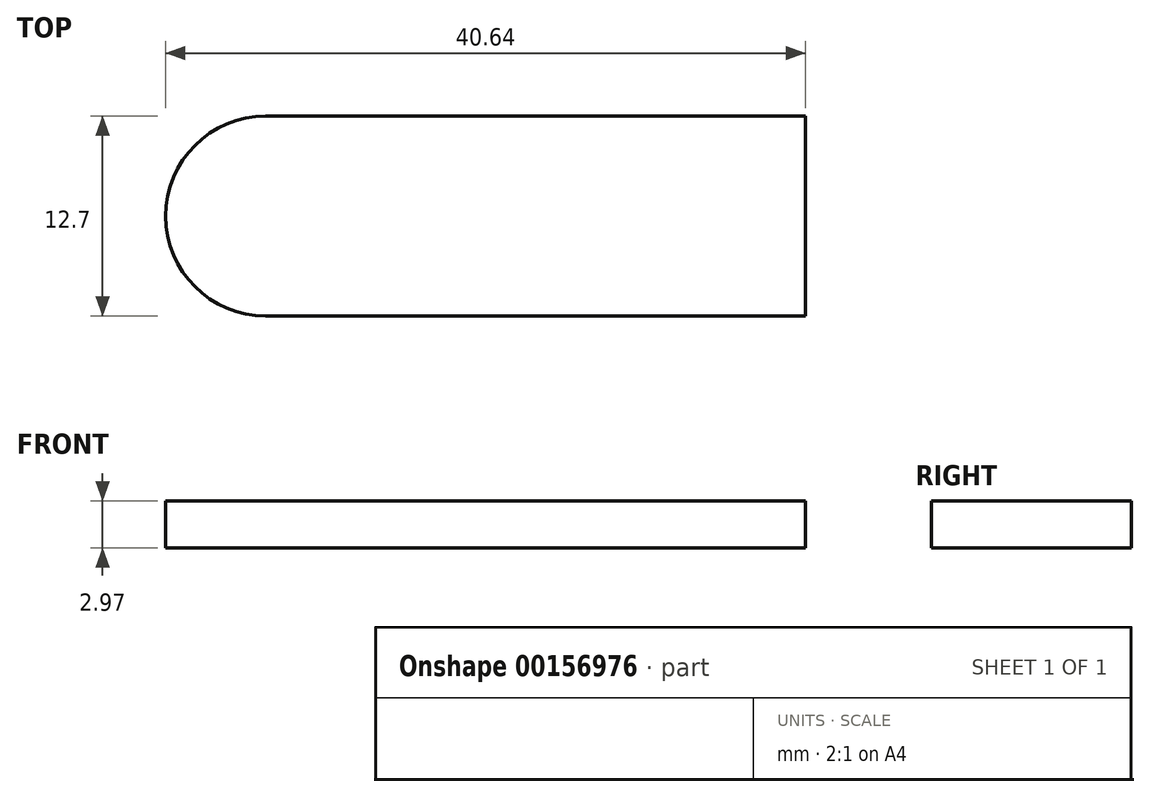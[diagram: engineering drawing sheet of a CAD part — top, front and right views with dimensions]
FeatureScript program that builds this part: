
annotation { "Feature Type Name" : "Feature", "Feature Type Description" : "" }
export const myFeature = defineFeature(function(context is Context, id is Id, definition is map)
    precondition{}
    {
        {
            var Q0;
            Q0=qCreatedBy(makeId("Top.planeOp"),FACE);
            var sketch = newSketch(context, id + "F0", { "sketchPlane" : qUnion([Q0])});
            skLineSegment(sketch, "E0.bottom", {"start": v(101.6, -57.15) * mm, "end": v(-101.6, -57.15) * mm});
            skLineSegment(sketch, "E0.top", {"start": v(101.6, 57.15) * mm, "end": v(-101.6, 57.15) * mm});
            skLineSegment(sketch, "E0.left", {"start": v(101.6, -57.15) * mm, "end": v(101.6, 57.15) * mm});
            skLineSegment(sketch, "E0.right", {"start": v(-101.6, -57.15) * mm, "end": v(-101.6, 57.15) * mm});
            skPoint(sketch, "E0.middle", {"position": v(0, 0) * mm});
            skLineSegment(sketch, "E1.bottom", {"start": v(88.9, -57.15) * mm, "end": v(78.74, -57.15) * mm});
            skLineSegment(sketch, "E1.top", {"start": v(88.9, -62.23) * mm, "end": v(78.74, -62.23) * mm});
            skLineSegment(sketch, "E1.left", {"start": v(88.9, -57.15) * mm, "end": v(88.9, -62.23) * mm});
            skLineSegment(sketch, "E1.right", {"start": v(78.74, -57.15) * mm, "end": v(78.74, -62.23) * mm});
            skLineSegment(sketch, "E2.1.0.0", {"start": v(12.7, -57.15) * mm, "end": v(12.7, -62.23) * mm});
            skLineSegment(sketch, "E2.1.0.1", {"start": v(12.7, -62.23) * mm, "end": v(2.54, -62.23) * mm});
            skLineSegment(sketch, "E2.1.0.2", {"start": v(2.54, -57.15) * mm, "end": v(2.54, -62.23) * mm});
            skLineSegment(sketch, "E2.1.0.3", {"start": v(12.7, -57.15) * mm, "end": v(2.54, -57.15) * mm});
            skLineSegment(sketch, "E2.2.0.0", {"start": v(-63.5, -57.15) * mm, "end": v(-63.5, -62.23) * mm});
            skLineSegment(sketch, "E2.2.0.1", {"start": v(-63.5, -62.23) * mm, "end": v(-73.66, -62.23) * mm});
            skLineSegment(sketch, "E2.2.0.2", {"start": v(-73.66, -57.15) * mm, "end": v(-73.66, -62.23) * mm});
            skLineSegment(sketch, "E2.2.0.3", {"start": v(-63.5, -57.15) * mm, "end": v(-73.66, -57.15) * mm});
            skLineSegment(sketch, "E2.direction1", {"start": v(88.9, -62.23) * mm, "end": v(12.7, -62.23) * mm, "construction": true});
            skLineSegment(sketch, "E3.MirrorCS", {"start": v(-63.5, 57.15) * mm, "end": v(-63.5, 62.23) * mm});
            skLineSegment(sketch, "E4.MirrorCS", {"start": v(-63.5, 62.23) * mm, "end": v(-73.66, 62.23) * mm});
            skLineSegment(sketch, "E5.MirrorCS", {"start": v(-73.66, 57.15) * mm, "end": v(-73.66, 62.23) * mm});
            skLineSegment(sketch, "E6.MirrorCS", {"start": v(2.54, 57.15) * mm, "end": v(2.54, 62.23) * mm});
            skLineSegment(sketch, "E7.MirrorCS", {"start": v(12.7, 62.23) * mm, "end": v(2.54, 62.23) * mm});
            skLineSegment(sketch, "E8.MirrorCS", {"start": v(12.7, 57.15) * mm, "end": v(12.7, 62.23) * mm});
            skLineSegment(sketch, "E9.MirrorCS", {"start": v(78.74, 57.15) * mm, "end": v(78.74, 62.23) * mm});
            skLineSegment(sketch, "E10.MirrorCS", {"start": v(88.9, 62.23) * mm, "end": v(12.7, 62.23) * mm, "construction": true});
            skLineSegment(sketch, "E11.MirrorCS", {"start": v(88.9, 57.15) * mm, "end": v(88.9, 62.23) * mm});
            skLineSegment(sketch, "E12", {"start": v(88.9, 62.23) * mm, "end": v(78.74, 62.23) * mm});
            skSolve(sketch);
        }
        {
            var Q0;
            Q0 = qSketchRegion(id + "F0", true);
            extrude(context, id + "F1", {"entities" : qUnion([Q0]), "depth" : 2.97 * mm});
        }
        {
            var Q0;
            Q0=makeQuery(id+"F1.opExtrude","CAP_FACE",FACE,{"disambiguationData":[OSD([sQuery(id+"F0.wireOp",EDGE,"E0.bottom"),sQuery(id+"F0.wireOp",EDGE,"E0.top"),sQuery(id+"F0.wireOp",EDGE,"E0.left"),sQuery(id+"F0.wireOp",EDGE,"E0.right"),sQuery(id+"F0.wireOp",EDGE,"E1.top"),sQuery(id+"F0.wireOp",EDGE,"E1.left"),sQuery(id+"F0.wireOp",EDGE,"E1.right"),sQuery(id+"F0.wireOp",EDGE,"E2.1.0.0"),sQuery(id+"F0.wireOp",EDGE,"E2.1.0.1"),sQuery(id+"F0.wireOp",EDGE,"E2.1.0.2"),sQuery(id+"F0.wireOp",EDGE,"E2.2.0.0"),sQuery(id+"F0.wireOp",EDGE,"E2.2.0.1"),sQuery(id+"F0.wireOp",EDGE,"E2.2.0.2"),sQuery(id+"F0.wireOp",EDGE,"E3.MirrorCS"),sQuery(id+"F0.wireOp",EDGE,"E4.MirrorCS"),sQuery(id+"F0.wireOp",EDGE,"E5.MirrorCS"),sQuery(id+"F0.wireOp",EDGE,"E6.MirrorCS"),sQuery(id+"F0.wireOp",EDGE,"E7.MirrorCS"),sQuery(id+"F0.wireOp",EDGE,"E8.MirrorCS"),sQuery(id+"F0.wireOp",EDGE,"E9.MirrorCS"),sQuery(id+"F0.wireOp",EDGE,"E11.MirrorCS"),sQuery(id+"F0.wireOp",EDGE,"E12")])],"isStart":false});
            var sketch = newSketch(context, id + "F2", { "sketchPlane" : qUnion([Q0])});
            skLineSegment(sketch, "E13", {"start": v(0, 0) * mm, "end": v(-101.6, 0) * mm, "construction": true});
            skLineSegment(sketch, "E14", {"start": v(12.7, -49.53) * mm, "end": v(71.12, -49.53) * mm});
            skArc(sketch, "E15.0.startCap", {"start": v(12.7, -54.61) * mm, "mid": v(7.62, -49.53) * mm, "end": v(12.7, -44.45) * mm});
            skArc(sketch, "E15.0.endCap", {"start": v(71.12, -44.45) * mm, "mid": v(76.2, -49.53) * mm, "end": v(71.12, -54.6) * mm});
            skLineSegment(sketch, "E15.0.left", {"start": v(12.7, -44.45) * mm, "end": v(71.12, -44.45) * mm});
            skLineSegment(sketch, "E15.0.right", {"start": v(12.7, -54.61) * mm, "end": v(71.12, -54.6) * mm});
            skLineSegment(sketch, "E16.MirrorCS", {"start": v(12.7, 44.45) * mm, "end": v(71.12, 44.45) * mm});
            skLineSegment(sketch, "E17.MirrorCS", {"start": v(12.7, 54.61) * mm, "end": v(71.12, 54.61) * mm});
            skArc(sketch, "E18.MirrorCS", {"start": v(12.7, 54.61) * mm, "mid": v(7.62, 49.53) * mm, "end": v(12.7, 44.45) * mm});
            skArc(sketch, "E19.MirrorCS", {"start": v(71.12, 44.45) * mm, "mid": v(76.2, 49.53) * mm, "end": v(71.12, 54.61) * mm});
            skLineSegment(sketch, "E20.MirrorCS", {"start": v(12.7, 49.53) * mm, "end": v(71.12, 49.53) * mm});
            skLineSegment(sketch, "E21", {"start": v(41.91, -49.53) * mm, "end": v(41.91, 0) * mm, "construction": true});
            skLineSegment(sketch, "E22.bottom", {"start": v(41.91, -44.45) * mm, "end": v(54.61, -44.45) * mm});
            skLineSegment(sketch, "E22.top", {"start": v(41.91, -36.83) * mm, "end": v(54.61, -36.83) * mm});
            skLineSegment(sketch, "E22.left", {"start": v(41.91, -44.45) * mm, "end": v(41.91, -36.83) * mm});
            skLineSegment(sketch, "E22.right", {"start": v(54.61, -44.45) * mm, "end": v(54.61, -36.83) * mm});
            skLineSegment(sketch, "E23.MirrorCS", {"start": v(29.2, -44.45) * mm, "end": v(29.2, -36.83) * mm});
            skLineSegment(sketch, "E24.MirrorCS", {"start": v(41.91, -36.83) * mm, "end": v(29.2, -36.83) * mm});
            skLineSegment(sketch, "E25", {"start": v(0, 0) * mm, "end": v(76.3, 0) * mm, "construction": true});
            skLineSegment(sketch, "E26.MirrorCS", {"start": v(41.91, 36.83) * mm, "end": v(29.2, 36.83) * mm});
            skLineSegment(sketch, "E27.MirrorCS", {"start": v(29.2, 44.45) * mm, "end": v(29.2, 36.83) * mm});
            skLineSegment(sketch, "E28.MirrorCS", {"start": v(41.91, 36.83) * mm, "end": v(54.61, 36.83) * mm});
            skLineSegment(sketch, "E29.MirrorCS", {"start": v(54.6, 44.45) * mm, "end": v(54.6, 36.83) * mm});
            skLineSegment(sketch, "E30", {"start": v(41.91, 0) * mm, "end": v(41.91, 36.83) * mm, "construction": true});
            skLineSegment(sketch, "E31.bottom", {"start": v(33.02, -15.88) * mm, "end": v(30.05, -15.88) * mm});
            skLineSegment(sketch, "E31.top", {"start": v(33.02, -22.23) * mm, "end": v(30.05, -22.23) * mm});
            skLineSegment(sketch, "E31.left", {"start": v(33.02, -15.88) * mm, "end": v(33.02, -22.23) * mm});
            skLineSegment(sketch, "E31.right", {"start": v(30.05, -15.88) * mm, "end": v(30.05, -22.23) * mm});
            skLineSegment(sketch, "E32.MirrorCS", {"start": v(53.77, -15.88) * mm, "end": v(53.77, -22.23) * mm});
            skLineSegment(sketch, "E33.MirrorCS", {"start": v(50.8, -15.88) * mm, "end": v(50.8, -22.23) * mm});
            skLineSegment(sketch, "E34.MirrorCS", {"start": v(50.8, -15.88) * mm, "end": v(53.77, -15.88) * mm});
            skLineSegment(sketch, "E35.MirrorCS", {"start": v(50.8, -22.23) * mm, "end": v(53.77, -22.23) * mm});
            skLineSegment(sketch, "E36.MirrorCS", {"start": v(30.05, 15.88) * mm, "end": v(30.05, 22.23) * mm});
            skLineSegment(sketch, "E37.MirrorCS", {"start": v(33.02, 15.88) * mm, "end": v(30.05, 15.88) * mm});
            skLineSegment(sketch, "E38.MirrorCS", {"start": v(33.02, 15.88) * mm, "end": v(33.02, 22.23) * mm});
            skLineSegment(sketch, "E39.MirrorCS", {"start": v(33.02, 22.23) * mm, "end": v(30.05, 22.23) * mm});
            skLineSegment(sketch, "E40.MirrorCS", {"start": v(50.8, 15.88) * mm, "end": v(53.77, 15.88) * mm});
            skLineSegment(sketch, "E41.MirrorCS", {"start": v(50.8, 15.88) * mm, "end": v(50.8, 22.23) * mm});
            skLineSegment(sketch, "E42.MirrorCS", {"start": v(53.77, 15.88) * mm, "end": v(53.77, 22.23) * mm});
            skLineSegment(sketch, "E43.MirrorCS", {"start": v(50.8, 22.23) * mm, "end": v(53.77, 22.23) * mm});
            skLineSegment(sketch, "E44", {"start": v(92.71, 0) * mm, "end": v(67.31, 0) * mm});
            skArc(sketch, "E45.0.endCap", {"start": v(67.31, -6.35) * mm, "mid": v(60.96, 0) * mm, "end": v(67.31, 6.35) * mm});
            skLineSegment(sketch, "E45.0.left", {"start": v(92.71, -6.35) * mm, "end": v(67.31, -6.35) * mm});
            skLineSegment(sketch, "E45.0.right", {"start": v(92.71, 6.35) * mm, "end": v(67.31, 6.35) * mm});
            skLineSegment(sketch, "E46", {"start": v(92.71, -6.35) * mm, "end": v(101.6, -6.35) * mm});
            skLineSegment(sketch, "E47", {"start": v(92.71, 6.35) * mm, "end": v(101.6, 6.35) * mm});
            skSolve(sketch);
        }
        {
            var Q0;
            Q0 = qSketchRegion(id + "F2", true);
            var Q1;
            Q1=makeQuery(id+"F2.imprint","IMPRINT",FACE,{"disambiguationData":[TD([[makeQuery(id+"F2.imprint","IMPRINT",EDGE,{"derivedFrom":sQuery(id+"F2.wireOp",EDGE,"E45.0.endCap")}),-1.0]])]});
            extrude(context, id + "F3", {"entities" : qUnion([Q0, Q1]), "operationType" : NewBodyOperationType.REMOVE, "endBound" : BoundingType.THROUGH_ALL, "oppositeDirection" : true, "depth" : 25.4 * mm});
        }
    });
